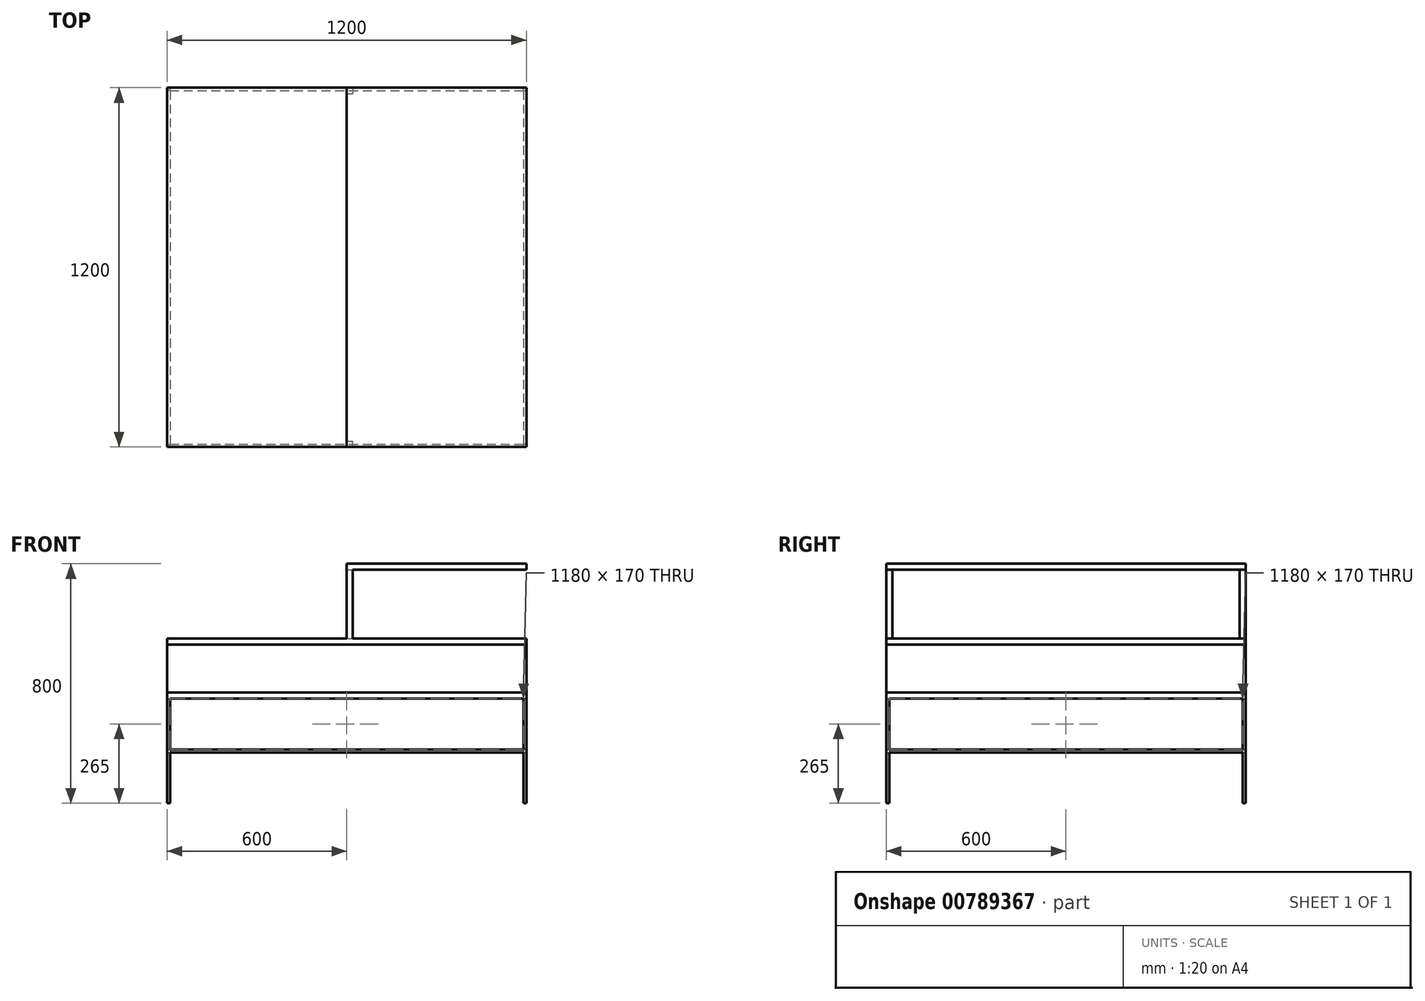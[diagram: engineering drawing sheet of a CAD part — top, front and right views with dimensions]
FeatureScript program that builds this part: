
annotation { "Feature Type Name" : "Feature", "Feature Type Description" : "" }
export const myFeature = defineFeature(function(context is Context, id is Id, definition is map)
    precondition{}
    {
        {
            var Q0;
            Q0=qCreatedBy(makeId("Top.planeOp"),FACE);
            var sketch = newSketch(context, id + "F0", { "sketchPlane" : qUnion([Q0])});
            skLineSegment(sketch, "E0.bottom", {"start": v(600, 600) * mm, "end": v(-600, 600) * mm, "construction": true});
            skLineSegment(sketch, "E0.top", {"start": v(600, -600) * mm, "end": v(-600, -600) * mm, "construction": true});
            skLineSegment(sketch, "E0.left", {"start": v(600, 600) * mm, "end": v(600, -600) * mm, "construction": true});
            skLineSegment(sketch, "E0.right", {"start": v(-600, 600) * mm, "end": v(-600, -600) * mm, "construction": true});
            skPoint(sketch, "E0.middle", {"position": v(0, 0) * mm});
            skLineSegment(sketch, "E1.bottom", {"start": v(-590, 590) * mm, "end": v(590, 590) * mm, "construction": true});
            skLineSegment(sketch, "E1.top", {"start": v(-590, -590) * mm, "end": v(590, -590) * mm, "construction": true});
            skLineSegment(sketch, "E1.left", {"start": v(-590, 590) * mm, "end": v(-590, -590) * mm, "construction": true});
            skLineSegment(sketch, "E1.right", {"start": v(590, 590) * mm, "end": v(590, -590) * mm, "construction": true});
            skLineSegment(sketch, "E2.bottom", {"start": v(-600, -600) * mm, "end": v(-590, -600) * mm});
            skLineSegment(sketch, "E2.top", {"start": v(-600, -590) * mm, "end": v(-590, -590) * mm});
            skLineSegment(sketch, "E2.left", {"start": v(-600, -600) * mm, "end": v(-600, -590) * mm});
            skLineSegment(sketch, "E2.right", {"start": v(-590, -600) * mm, "end": v(-590, -590) * mm});
            skLineSegment(sketch, "E3.bottom", {"start": v(600, -600) * mm, "end": v(590, -600) * mm});
            skLineSegment(sketch, "E3.top", {"start": v(600, -590) * mm, "end": v(590, -590) * mm});
            skLineSegment(sketch, "E3.left", {"start": v(600, -600) * mm, "end": v(600, -590) * mm});
            skLineSegment(sketch, "E3.right", {"start": v(590, -600) * mm, "end": v(590, -590) * mm});
            skLineSegment(sketch, "E4.bottom", {"start": v(590, 590) * mm, "end": v(600, 590) * mm});
            skLineSegment(sketch, "E4.top", {"start": v(590, 600) * mm, "end": v(600, 600) * mm});
            skLineSegment(sketch, "E4.left", {"start": v(590, 590) * mm, "end": v(590, 600) * mm});
            skLineSegment(sketch, "E4.right", {"start": v(600, 590) * mm, "end": v(600, 600) * mm});
            skLineSegment(sketch, "E5.bottom", {"start": v(-590, 590) * mm, "end": v(-600, 590) * mm});
            skLineSegment(sketch, "E5.top", {"start": v(-590, 600) * mm, "end": v(-600, 600) * mm});
            skLineSegment(sketch, "E5.left", {"start": v(-590, 590) * mm, "end": v(-590, 600) * mm});
            skLineSegment(sketch, "E5.right", {"start": v(-600, 590) * mm, "end": v(-600, 600) * mm});
            skSolve(sketch);
        }
        {
            var Q0;
            Q0=makeQuery(id+"F0.imprint","IMPRINT",FACE,{"disambiguationData":[TD([[makeQuery(id+"F0.imprint","IMPRINT",EDGE,{"derivedFrom":sQuery(id+"F0.wireOp",EDGE,"E5.bottom")}),-1.0]])]});
            var Q1;
            Q1=makeQuery(id+"F0.imprint","IMPRINT",FACE,{"disambiguationData":[TD([[makeQuery(id+"F0.imprint","IMPRINT",EDGE,{"derivedFrom":sQuery(id+"F0.wireOp",EDGE,"E4.bottom")}),1.0]])]});
            var Q2;
            Q2=makeQuery(id+"F0.imprint","IMPRINT",FACE,{"disambiguationData":[TD([[makeQuery(id+"F0.imprint","IMPRINT",EDGE,{"derivedFrom":sQuery(id+"F0.wireOp",EDGE,"E3.bottom")}),-1.0]])]});
            var Q3;
            Q3=makeQuery(id+"F0.imprint","IMPRINT",FACE,{"disambiguationData":[TD([[makeQuery(id+"F0.imprint","IMPRINT",EDGE,{"derivedFrom":sQuery(id+"F0.wireOp",EDGE,"E2.bottom")}),1.0]])]});
            extrude(context, id + "F1", {"entities" : qUnion([Q0, Q1, Q2, Q3]), "depth" : 350 * mm, "offsetDistance" : 25 * mm});
        }
        {
            var Q0;
            Q0=qCreatedBy(makeId("Top.planeOp"),FACE);
            cPlane(context, id + "F2", {"entities" : qUnion([Q0]), "cplaneType" : CPlaneType.OFFSET, "offset" : (350 / 2) * mm, "width" : 150 * mm, "height" : 150 * mm});
        }
        {
            var Q0;
            Q0=qCreatedBy(id+"F2.planeOp",FACE);
            var sketch = newSketch(context, id + "F3", { "sketchPlane" : qUnion([Q0])});
            skLineSegment(sketch, "E6.bottom", {"start": v(600, 600) * mm, "end": v(-600, 600) * mm});
            skLineSegment(sketch, "E6.top", {"start": v(600, -600) * mm, "end": v(-600, -600) * mm});
            skLineSegment(sketch, "E6.left", {"start": v(600, 600) * mm, "end": v(600, -600) * mm});
            skLineSegment(sketch, "E6.right", {"start": v(-600, 600) * mm, "end": v(-600, -600) * mm});
            skLineSegment(sketch, "E7.bottom", {"start": v(-590, 590) * mm, "end": v(590, 590) * mm});
            skLineSegment(sketch, "E7.top", {"start": v(-590, -590) * mm, "end": v(590, -590) * mm});
            skLineSegment(sketch, "E7.left", {"start": v(-590, 590) * mm, "end": v(-590, -590) * mm});
            skLineSegment(sketch, "E7.right", {"start": v(590, 590) * mm, "end": v(590, -590) * mm});
            skLineSegment(sketch, "E8", {"start": v(-600, -600) * mm, "end": v(600, 600) * mm, "construction": true});
            skLineSegment(sketch, "E9", {"start": v(600, -600) * mm, "end": v(-600, 600) * mm, "construction": true});
            skPoint(sketch, "E10", {"position": v(0, 0) * mm});
            skLineSegment(sketch, "E11", {"start": v(590, -590) * mm, "end": v(-590, 590) * mm, "construction": true});
            skSolve(sketch);
        }
        {
            var Q0;
            Q0=makeQuery(id+"F3.imprint","IMPRINT",FACE,{"disambiguationData":[TD([[makeQuery(id+"F3.imprint","IMPRINT",EDGE,{"derivedFrom":sQuery(id+"F3.wireOp",EDGE,"E6.bottom")}),1.0]])]});
            extrude(context, id + "F4", {"entities" : qUnion([Q0]), "operationType" : NewBodyOperationType.ADD, "endBound" : BoundingType.SYMMETRIC, "depth" : 10 * mm, "offsetDistance" : 25 * mm});
        }
        {
            var Q0;
            Q0=qCreatedBy(makeId("Top.planeOp"),FACE);
            cPlane(context, id + "F5", {"entities" : qUnion([Q0]), "cplaneType" : CPlaneType.OFFSET, "offset" : 350 * mm, "width" : 150 * mm, "height" : 150 * mm});
        }
        {
            var Q0;
            Q0=qCreatedBy(id+"F5.planeOp",FACE);
            var sketch = newSketch(context, id + "F6", { "sketchPlane" : qUnion([Q0])});
            skLineSegment(sketch, "E12.bottom", {"start": v(-600, 600) * mm, "end": v(600, 600) * mm});
            skLineSegment(sketch, "E12.top", {"start": v(-600, -600) * mm, "end": v(600, -600) * mm});
            skLineSegment(sketch, "E12.left", {"start": v(-600, 600) * mm, "end": v(-600, -600) * mm});
            skLineSegment(sketch, "E12.right", {"start": v(600, 600) * mm, "end": v(600, -600) * mm});
            skPoint(sketch, "E12.middle", {"position": v(0, 0) * mm});
            skSolve(sketch);
        }
        {
            var Q0;
            Q0=makeQuery(id+"F6.imprint","IMPRINT",FACE,{"disambiguationData":[TD([[makeQuery(id+"F6.imprint","IMPRINT",EDGE,{"derivedFrom":sQuery(id+"F6.wireOp",EDGE,"E12.bottom")}),-1.0]])]});
            extrude(context, id + "F7", {"entities" : qUnion([Q0]), "operationType" : NewBodyOperationType.ADD, "depth" : 20 * mm, "offsetDistance" : 25 * mm});
        }
        {
            var Q0;
            Q0=makeQuery(id+"F7.opExtrude","CAP_FACE",FACE,{"disambiguationData":[OSD([sQuery(id+"F6.wireOp",EDGE,"E12.bottom"),sQuery(id+"F6.wireOp",EDGE,"E12.top"),sQuery(id+"F6.wireOp",EDGE,"E12.left"),sQuery(id+"F6.wireOp",EDGE,"E12.right")])],"isStart":false});
            extrude(context, id + "F8", {"entities" : qUnion([Q0]), "depth" : 160 * mm, "offsetDistance" : 25 * mm});
        }
        {
            var Q0;
            Q0=makeQuery(id+"F8.opExtrude","CAP_FACE",FACE,{"disambiguationData":[OSD([sQuery(id+"F6.wireOp",EDGE,"E12.bottom"),sQuery(id+"F6.wireOp",EDGE,"E12.top"),sQuery(id+"F6.wireOp",EDGE,"E12.left"),sQuery(id+"F6.wireOp",EDGE,"E12.right")])],"isStart":false});
            extrude(context, id + "F9", {"entities" : qUnion([Q0]), "depth" : 20 * mm, "offsetDistance" : 25 * mm});
        }
        {
            var Q0;
            Q0=makeQuery(id+"F9.opExtrude","CAP_FACE",FACE,{"disambiguationData":[OSD([sQuery(id+"F6.wireOp",EDGE,"E12.bottom"),sQuery(id+"F6.wireOp",EDGE,"E12.top"),sQuery(id+"F6.wireOp",EDGE,"E12.left"),sQuery(id+"F6.wireOp",EDGE,"E12.right")])],"isStart":false});
            var sketch = newSketch(context, id + "F10", { "sketchPlane" : qUnion([Q0])});
            skLineSegment(sketch, "E13.bottom", {"start": v(600, 600) * mm, "end": v(0, 600) * mm, "construction": true});
            skLineSegment(sketch, "E13.top", {"start": v(600, -600) * mm, "end": v(0, -600) * mm, "construction": true});
            skLineSegment(sketch, "E13.left", {"start": v(600, 600) * mm, "end": v(600, -600) * mm, "construction": true});
            skLineSegment(sketch, "E13.right", {"start": v(0, 600) * mm, "end": v(0, -600) * mm, "construction": true});
            skLineSegment(sketch, "E14.bottom", {"start": v(0, 600) * mm, "end": v(20, 600) * mm});
            skLineSegment(sketch, "E14.top", {"start": v(0, 580) * mm, "end": v(20, 580) * mm});
            skLineSegment(sketch, "E14.left", {"start": v(0, 600) * mm, "end": v(0, 580) * mm});
            skLineSegment(sketch, "E14.right", {"start": v(20, 600) * mm, "end": v(20, 580) * mm});
            skLineSegment(sketch, "E15.bottom", {"start": v(0, -600) * mm, "end": v(20, -600) * mm});
            skLineSegment(sketch, "E15.top", {"start": v(0, -580) * mm, "end": v(20, -580) * mm});
            skLineSegment(sketch, "E15.left", {"start": v(0, -600) * mm, "end": v(0, -580) * mm});
            skLineSegment(sketch, "E15.right", {"start": v(20, -600) * mm, "end": v(20, -580) * mm});
            skSolve(sketch);
        }
        {
            var Q0;
            Q0=makeQuery(id+"F10.imprint","IMPRINT",FACE,{"disambiguationData":[TD([[makeQuery(id+"F10.imprint","IMPRINT",EDGE,{"derivedFrom":sQuery(id+"F10.wireOp",EDGE,"E14.bottom")}),-1.0]])]});
            var Q1;
            Q1=makeQuery(id+"F10.imprint","IMPRINT",FACE,{"disambiguationData":[TD([[makeQuery(id+"F10.imprint","IMPRINT",EDGE,{"derivedFrom":sQuery(id+"F10.wireOp",EDGE,"E15.bottom")}),1.0]])]});
            extrude(context, id + "F11", {"entities" : qUnion([Q0, Q1]), "operationType" : NewBodyOperationType.ADD, "depth" : 250 * mm, "offsetDistance" : 25 * mm});
        }
        {
            var Q0;
            Q0=makeQuery(id+"F11.opExtrude","SWEPT_FACE",FACE,{"disambiguationData":[OSD([sQuery(id+"F10.wireOp",EDGE,"E14.right")])]});
            cPlane(context, id + "F12", {"entities" : qUnion([Q0]), "cplaneType" : CPlaneType.OFFSET, "offset" : 20 * mm, "oppositeDirection" : true, "width" : 150 * mm, "height" : 150 * mm});
        }
        {
            var Q0;
            Q0=qCreatedBy(id+"F12.planeOp",FACE);
            var sketch = newSketch(context, id + "F13", { "sketchPlane" : qUnion([Q0])});
            skLineSegment(sketch, "E16.bottom", {"start": v(-600, 800) * mm, "end": v(600, 800) * mm});
            skLineSegment(sketch, "E16.top", {"start": v(-600, 780) * mm, "end": v(600, 780) * mm});
            skLineSegment(sketch, "E16.left", {"start": v(-600, 800) * mm, "end": v(-600, 780) * mm});
            skLineSegment(sketch, "E16.right", {"start": v(600, 800) * mm, "end": v(600, 780) * mm});
            skSolve(sketch);
        }
        {
            var Q0;
            Q0=makeQuery(id+"F13.imprint","IMPRINT",FACE,{"disambiguationData":[TD([[makeQuery(id+"F13.imprint","IMPRINT",EDGE,{"derivedFrom":sQuery(id+"F13.wireOp",EDGE,"E16.bottom")}),-1.0]])]});
            extrude(context, id + "F14", {"entities" : qUnion([Q0]), "operationType" : NewBodyOperationType.ADD, "depth" : 600 * mm, "offsetDistance" : 25 * mm});
        }
    });
